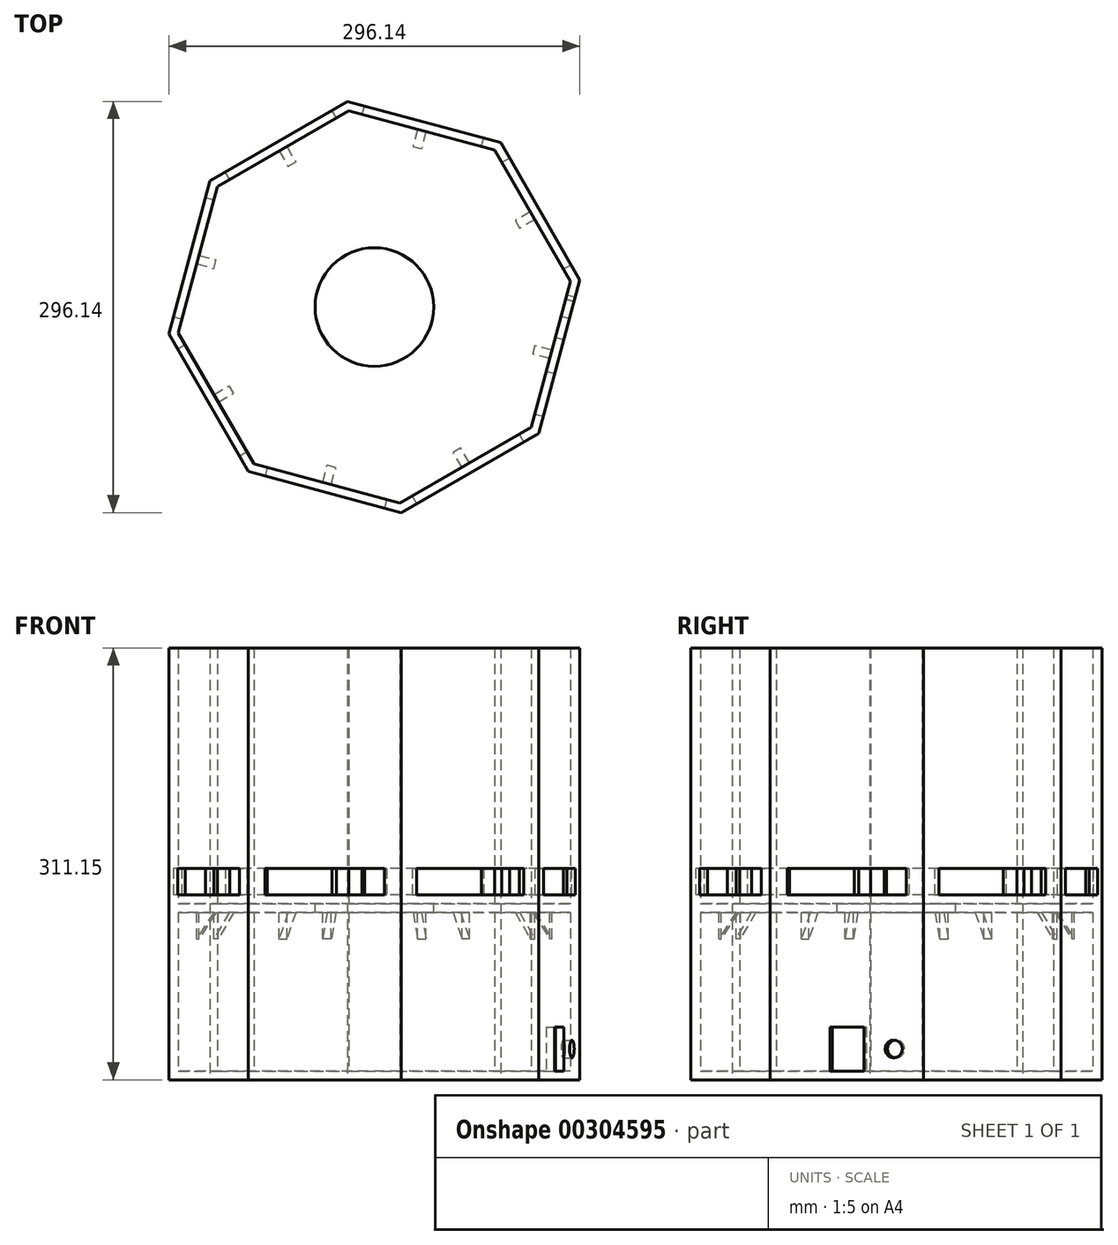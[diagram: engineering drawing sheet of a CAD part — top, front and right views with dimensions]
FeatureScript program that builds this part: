
annotation { "Feature Type Name" : "Feature", "Feature Type Description" : "" }
export const myFeature = defineFeature(function(context is Context, id is Id, definition is map)
    precondition{}
    {
        {
            var Q0;
            Q0=qCreatedBy(makeId("Top.planeOp"),FACE);
            var sketch = newSketch(context, id + "F0", { "sketchPlane" : qUnion([Q0])});
            skCircle(sketch, "E0.cCircle", {"center": v(0, 0) * mm, "radius": 137.97 * mm, "construction": true});
            skLineSegment(sketch, "E0.0", {"start": v(118.45, -90.95) * mm, "end": v(19.44, -148.07) * mm});
            skLineSegment(sketch, "E0.1", {"start": v(19.44, -148.07) * mm, "end": v(-90.95, -118.45) * mm});
            skLineSegment(sketch, "E0.2", {"start": v(-90.95, -118.45) * mm, "end": v(-148.07, -19.44) * mm});
            skLineSegment(sketch, "E0.3", {"start": v(-148.07, -19.44) * mm, "end": v(-118.45, 90.95) * mm});
            skLineSegment(sketch, "E0.4", {"start": v(-118.45, 90.95) * mm, "end": v(-19.44, 148.07) * mm});
            skLineSegment(sketch, "E0.5", {"start": v(-19.44, 148.07) * mm, "end": v(90.95, 118.45) * mm});
            skLineSegment(sketch, "E0.6", {"start": v(90.95, 118.45) * mm, "end": v(148.07, 19.44) * mm});
            skLineSegment(sketch, "E0.7", {"start": v(148.07, 19.44) * mm, "end": v(118.45, -90.95) * mm});
            skPoint(sketch, "E0.0.midPoint", {"position": v(68.94, -119.51) * mm});
            skCircle(sketch, "E1.cCircle", {"center": v(0, 0) * mm, "radius": 131.62 * mm, "construction": true});
            skLineSegment(sketch, "E1.0", {"start": v(113, -86.77) * mm, "end": v(18.55, -141.25) * mm});
            skLineSegment(sketch, "E1.1", {"start": v(18.55, -141.25) * mm, "end": v(-86.77, -113) * mm});
            skLineSegment(sketch, "E1.2", {"start": v(-86.77, -113) * mm, "end": v(-141.25, -18.55) * mm});
            skLineSegment(sketch, "E1.3", {"start": v(-141.25, -18.55) * mm, "end": v(-113, 86.77) * mm});
            skLineSegment(sketch, "E1.4", {"start": v(-113, 86.77) * mm, "end": v(-18.55, 141.25) * mm});
            skLineSegment(sketch, "E1.5", {"start": v(-18.55, 141.25) * mm, "end": v(86.77, 113) * mm});
            skLineSegment(sketch, "E1.6", {"start": v(86.77, 113) * mm, "end": v(141.25, 18.55) * mm});
            skLineSegment(sketch, "E1.7", {"start": v(141.25, 18.55) * mm, "end": v(113, -86.77) * mm});
            skPoint(sketch, "E1.0.midPoint", {"position": v(65.77, -114.01) * mm});
            skLineSegment(sketch, "E2", {"start": v(-19.44, 148.07) * mm, "end": v(0, 0) * mm});
            skSolve(sketch);
        }
        {
            var Q0;
            Q0=makeQuery(id+"F0.imprint","IMPRINT",FACE,{"disambiguationData":[TD([[makeQuery(id+"F0.imprint","IMPRINT",EDGE,{"derivedFrom":sQuery(id+"F0.wireOp",EDGE,"E1.0")}),-1.0]])]});
            cPlane(context, id + "F1", {"entities" : qUnion([Q0]), "cplaneType" : CPlaneType.OFFSET, "offset" : 120.65 * mm, "width" : 152.4 * mm, "height" : 152.4 * mm});
        }
        {
            var Q0;
            Q0=qCreatedBy(id+"F1.planeOp",FACE);
            var sketch = newSketch(context, id + "F2", { "sketchPlane" : qUnion([Q0])});
            skCircle(sketch, "E3.cCircle", {"center": v(0, 0) * mm, "radius": 137.97 * mm, "construction": true});
            skLineSegment(sketch, "E3.0", {"start": v(118.45, -90.95) * mm, "end": v(19.44, -148.07) * mm});
            skLineSegment(sketch, "E3.1", {"start": v(19.44, -148.07) * mm, "end": v(-90.95, -118.45) * mm});
            skLineSegment(sketch, "E3.2", {"start": v(-90.95, -118.45) * mm, "end": v(-148.07, -19.44) * mm});
            skLineSegment(sketch, "E3.3", {"start": v(-148.07, -19.44) * mm, "end": v(-118.45, 90.95) * mm});
            skLineSegment(sketch, "E3.4", {"start": v(-118.45, 90.95) * mm, "end": v(-19.44, 148.07) * mm});
            skLineSegment(sketch, "E3.5", {"start": v(-19.44, 148.07) * mm, "end": v(90.95, 118.45) * mm});
            skLineSegment(sketch, "E3.6", {"start": v(90.95, 118.45) * mm, "end": v(148.07, 19.44) * mm});
            skLineSegment(sketch, "E3.7", {"start": v(148.07, 19.44) * mm, "end": v(118.45, -90.95) * mm});
            skPoint(sketch, "E3.0.midPoint", {"position": v(68.94, -119.51) * mm});
            skCircle(sketch, "E4.cCircle", {"center": v(0, 0) * mm, "radius": 131.62 * mm, "construction": true});
            skLineSegment(sketch, "E4.0", {"start": v(113, -86.77) * mm, "end": v(18.55, -141.25) * mm});
            skLineSegment(sketch, "E4.1", {"start": v(18.55, -141.25) * mm, "end": v(-86.77, -113) * mm});
            skLineSegment(sketch, "E4.2", {"start": v(-86.77, -113) * mm, "end": v(-141.25, -18.55) * mm});
            skLineSegment(sketch, "E4.3", {"start": v(-141.25, -18.55) * mm, "end": v(-113, 86.77) * mm});
            skLineSegment(sketch, "E4.4", {"start": v(-113, 86.77) * mm, "end": v(-18.55, 141.25) * mm});
            skLineSegment(sketch, "E4.5", {"start": v(-18.55, 141.25) * mm, "end": v(86.77, 113) * mm});
            skLineSegment(sketch, "E4.6", {"start": v(86.77, 113) * mm, "end": v(141.25, 18.55) * mm});
            skLineSegment(sketch, "E4.7", {"start": v(141.25, 18.55) * mm, "end": v(113, -86.77) * mm});
            skPoint(sketch, "E4.0.midPoint", {"position": v(65.77, -114.01) * mm});
            skLineSegment(sketch, "E5", {"start": v(-19.44, 148.07) * mm, "end": v(0, 0) * mm});
            skSolve(sketch);
        }
        {
            var Q0;
            Q0=makeQuery(id+"F2.imprint","IMPRINT",FACE,{"disambiguationData":[TD([[makeQuery(id+"F2.imprint","IMPRINT",EDGE,{"derivedFrom":sQuery(id+"F2.wireOp",EDGE,"E4.0")}),-1.0]])]});
            extrude(context, id + "F3", {"entities" : qUnion([Q0]), "depth" : 6.35 * mm});
        }
        {
            var Q0;
            Q0=makeQuery(id+"F0.imprint","IMPRINT",FACE,{"disambiguationData":[TD([[makeQuery(id+"F0.imprint","IMPRINT",EDGE,{"derivedFrom":sQuery(id+"F0.wireOp",EDGE,"E1.0")}),-1.0]])]});
            extrude(context, id + "F4", {"entities" : qUnion([Q0]), "depth" : 6.35 * mm});
        }
        {
            var Q0;
            Q0=makeQuery(id+"F0.imprint","IMPRINT",FACE,{"disambiguationData":[TD([[makeQuery(id+"F0.imprint","IMPRINT",EDGE,{"derivedFrom":sQuery(id+"F0.wireOp",EDGE,"E0.0")}),-1.0]])]});
            extrude(context, id + "F5", {"entities" : qUnion([Q0]), "operationType" : NewBodyOperationType.ADD, "depth" : 311.15 * mm});
        }
        {
            var Q0;
            Q0=makeQuery(id+"F5.opExtrude","SWEPT_FACE",FACE,{"disambiguationData":[OSD([sQuery(id+"F0.wireOp",EDGE,"E0.1")])]});
            var sketch = newSketch(context, id + "F6", { "sketchPlane" : qUnion([Q0])});
            skLineSegment(sketch, "E6.bottom", {"start": v(-44.45, 152.4) * mm, "end": v(44.45, 152.4) * mm});
            skLineSegment(sketch, "E6.top", {"start": v(-44.45, 133.35) * mm, "end": v(44.45, 133.35) * mm});
            skLineSegment(sketch, "E6.left", {"start": v(-44.45, 152.4) * mm, "end": v(-44.45, 133.35) * mm});
            skLineSegment(sketch, "E6.right", {"start": v(44.45, 152.4) * mm, "end": v(44.45, 133.35) * mm});
            skSolve(sketch);
        }
        {
            var Q0;
            Q0=makeQuery(id+"F5.opExtrude","SWEPT_FACE",FACE,{"disambiguationData":[OSD([sQuery(id+"F0.wireOp",EDGE,"E0.2")])]});
            var sketch = newSketch(context, id + "F7", { "sketchPlane" : qUnion([Q0])});
            skLineSegment(sketch, "E7.bottom", {"start": v(-44.45, 152.4) * mm, "end": v(44.45, 152.4) * mm});
            skLineSegment(sketch, "E7.top", {"start": v(-44.45, 133.35) * mm, "end": v(44.45, 133.35) * mm});
            skLineSegment(sketch, "E7.left", {"start": v(-44.45, 152.4) * mm, "end": v(-44.45, 133.35) * mm});
            skLineSegment(sketch, "E7.right", {"start": v(44.45, 152.4) * mm, "end": v(44.45, 133.35) * mm});
            skSolve(sketch);
        }
        {
            var Q0;
            Q0=makeQuery(id+"F5.opExtrude","SWEPT_FACE",FACE,{"disambiguationData":[OSD([sQuery(id+"F0.wireOp",EDGE,"E0.3")])]});
            var sketch = newSketch(context, id + "F8", { "sketchPlane" : qUnion([Q0])});
            skLineSegment(sketch, "E8.bottom", {"start": v(-44.45, 152.4) * mm, "end": v(44.45, 152.4) * mm});
            skLineSegment(sketch, "E8.top", {"start": v(-44.45, 133.35) * mm, "end": v(44.45, 133.35) * mm});
            skLineSegment(sketch, "E8.left", {"start": v(-44.45, 152.4) * mm, "end": v(-44.45, 133.35) * mm});
            skLineSegment(sketch, "E8.right", {"start": v(44.45, 152.4) * mm, "end": v(44.45, 133.35) * mm});
            skSolve(sketch);
        }
        {
            var Q0;
            Q0=makeQuery(id+"F5.opExtrude","SWEPT_FACE",FACE,{"disambiguationData":[OSD([sQuery(id+"F0.wireOp",EDGE,"E0.4")])]});
            var sketch = newSketch(context, id + "F9", { "sketchPlane" : qUnion([Q0])});
            skLineSegment(sketch, "E9.bottom", {"start": v(-44.45, 152.4) * mm, "end": v(44.45, 152.4) * mm});
            skLineSegment(sketch, "E9.top", {"start": v(-44.45, 133.35) * mm, "end": v(44.45, 133.35) * mm});
            skLineSegment(sketch, "E9.left", {"start": v(-44.45, 152.4) * mm, "end": v(-44.45, 133.35) * mm});
            skLineSegment(sketch, "E9.right", {"start": v(44.45, 152.4) * mm, "end": v(44.45, 133.35) * mm});
            skSolve(sketch);
        }
        {
            var Q0;
            Q0=makeQuery(id+"F5.opExtrude","SWEPT_FACE",FACE,{"disambiguationData":[OSD([sQuery(id+"F0.wireOp",EDGE,"E0.5")])]});
            var sketch = newSketch(context, id + "F10", { "sketchPlane" : qUnion([Q0])});
            skLineSegment(sketch, "E10.bottom", {"start": v(-44.45, 152.4) * mm, "end": v(44.45, 152.4) * mm});
            skLineSegment(sketch, "E10.top", {"start": v(-44.45, 133.35) * mm, "end": v(44.45, 133.35) * mm});
            skLineSegment(sketch, "E10.left", {"start": v(-44.45, 152.4) * mm, "end": v(-44.45, 133.35) * mm});
            skLineSegment(sketch, "E10.right", {"start": v(44.45, 152.4) * mm, "end": v(44.45, 133.35) * mm});
            skSolve(sketch);
        }
        {
            var Q0;
            Q0=makeQuery(id+"F5.opExtrude","SWEPT_FACE",FACE,{"disambiguationData":[OSD([sQuery(id+"F0.wireOp",EDGE,"E0.6")])]});
            var sketch = newSketch(context, id + "F11", { "sketchPlane" : qUnion([Q0])});
            skLineSegment(sketch, "E11.bottom", {"start": v(-44.45, 152.4) * mm, "end": v(44.45, 152.4) * mm});
            skLineSegment(sketch, "E11.top", {"start": v(-44.45, 133.35) * mm, "end": v(44.45, 133.35) * mm});
            skLineSegment(sketch, "E11.left", {"start": v(-44.45, 152.4) * mm, "end": v(-44.45, 133.35) * mm});
            skLineSegment(sketch, "E11.right", {"start": v(44.45, 152.4) * mm, "end": v(44.45, 133.35) * mm});
            skSolve(sketch);
        }
        {
            var Q0;
            Q0=makeQuery(id+"F5.opExtrude","SWEPT_FACE",FACE,{"disambiguationData":[OSD([sQuery(id+"F0.wireOp",EDGE,"E0.7")])]});
            var sketch = newSketch(context, id + "F12", { "sketchPlane" : qUnion([Q0])});
            skLineSegment(sketch, "E12.bottom", {"start": v(-44.45, 152.4) * mm, "end": v(44.45, 152.4) * mm});
            skLineSegment(sketch, "E12.top", {"start": v(-44.45, 133.35) * mm, "end": v(44.45, 133.35) * mm});
            skLineSegment(sketch, "E12.left", {"start": v(-44.45, 152.4) * mm, "end": v(-44.45, 133.35) * mm});
            skLineSegment(sketch, "E12.right", {"start": v(44.45, 152.4) * mm, "end": v(44.45, 133.35) * mm});
            skSolve(sketch);
        }
        {
            var Q0;
            Q0=makeQuery(id+"F5.opExtrude","SWEPT_FACE",FACE,{"disambiguationData":[OSD([sQuery(id+"F0.wireOp",EDGE,"E0.0")])]});
            var sketch = newSketch(context, id + "F13", { "sketchPlane" : qUnion([Q0])});
            skLineSegment(sketch, "E13.bottom", {"start": v(-44.45, 152.4) * mm, "end": v(44.45, 152.4) * mm});
            skLineSegment(sketch, "E13.top", {"start": v(-44.45, 133.35) * mm, "end": v(44.45, 133.35) * mm});
            skLineSegment(sketch, "E13.left", {"start": v(-44.45, 152.4) * mm, "end": v(-44.45, 133.35) * mm});
            skLineSegment(sketch, "E13.right", {"start": v(44.45, 152.4) * mm, "end": v(44.45, 133.35) * mm});
            skSolve(sketch);
        }
        {
            var Q0;
            Q0=makeQuery(id+"F13.imprint","IMPRINT",FACE,{"disambiguationData":[TD([[makeQuery(id+"F13.imprint","IMPRINT",EDGE,{"derivedFrom":sQuery(id+"F13.wireOp",EDGE,"E13.bottom")}),-1.0]])]});
            extrude(context, id + "F14", {"entities" : qUnion([Q0]), "operationType" : NewBodyOperationType.REMOVE, "oppositeDirection" : true, "depth" : 25.4 * mm});
        }
        {
            var Q0;
            Q0=makeQuery(id+"F12.imprint","IMPRINT",FACE,{"disambiguationData":[TD([[makeQuery(id+"F12.imprint","IMPRINT",EDGE,{"derivedFrom":sQuery(id+"F12.wireOp",EDGE,"E12.bottom")}),-1.0]])]});
            extrude(context, id + "F15", {"entities" : qUnion([Q0]), "operationType" : NewBodyOperationType.REMOVE, "oppositeDirection" : true, "depth" : 25.4 * mm});
        }
        {
            var Q0;
            Q0=makeQuery(id+"F11.imprint","IMPRINT",FACE,{"disambiguationData":[TD([[makeQuery(id+"F11.imprint","IMPRINT",EDGE,{"derivedFrom":sQuery(id+"F11.wireOp",EDGE,"E11.bottom")}),-1.0]])]});
            extrude(context, id + "F16", {"entities" : qUnion([Q0]), "operationType" : NewBodyOperationType.REMOVE, "oppositeDirection" : true, "depth" : 25.4 * mm});
        }
        {
            var Q0;
            Q0=makeQuery(id+"F10.imprint","IMPRINT",FACE,{"disambiguationData":[TD([[makeQuery(id+"F10.imprint","IMPRINT",EDGE,{"derivedFrom":sQuery(id+"F10.wireOp",EDGE,"E10.bottom")}),-1.0]])]});
            extrude(context, id + "F17", {"entities" : qUnion([Q0]), "operationType" : NewBodyOperationType.REMOVE, "oppositeDirection" : true, "depth" : 25.4 * mm});
        }
        {
            var Q0;
            Q0=makeQuery(id+"F9.imprint","IMPRINT",FACE,{"disambiguationData":[TD([[makeQuery(id+"F9.imprint","IMPRINT",EDGE,{"derivedFrom":sQuery(id+"F9.wireOp",EDGE,"E9.bottom")}),-1.0]])]});
            extrude(context, id + "F18", {"entities" : qUnion([Q0]), "operationType" : NewBodyOperationType.REMOVE, "oppositeDirection" : true, "depth" : 25.4 * mm});
        }
        {
            var Q0;
            Q0=makeQuery(id+"F8.imprint","IMPRINT",FACE,{"disambiguationData":[TD([[makeQuery(id+"F8.imprint","IMPRINT",EDGE,{"derivedFrom":sQuery(id+"F8.wireOp",EDGE,"E8.bottom")}),-1.0]])]});
            extrude(context, id + "F19", {"entities" : qUnion([Q0]), "operationType" : NewBodyOperationType.REMOVE, "oppositeDirection" : true, "depth" : 25.4 * mm});
        }
        {
            var Q0;
            Q0=makeQuery(id+"F7.imprint","IMPRINT",FACE,{"disambiguationData":[TD([[makeQuery(id+"F7.imprint","IMPRINT",EDGE,{"derivedFrom":sQuery(id+"F7.wireOp",EDGE,"E7.bottom")}),-1.0]])]});
            extrude(context, id + "F20", {"entities" : qUnion([Q0]), "operationType" : NewBodyOperationType.REMOVE, "oppositeDirection" : true, "depth" : 25.4 * mm});
        }
        {
            var Q0;
            Q0=makeQuery(id+"F6.imprint","IMPRINT",FACE,{"disambiguationData":[TD([[makeQuery(id+"F6.imprint","IMPRINT",EDGE,{"derivedFrom":sQuery(id+"F6.wireOp",EDGE,"E6.bottom")}),-1.0]])]});
            extrude(context, id + "F21", {"entities" : qUnion([Q0]), "operationType" : NewBodyOperationType.REMOVE, "oppositeDirection" : true, "depth" : 25.4 * mm});
        }
        {
            var Q0;
            Q0=makeQuery(id+"F3.opExtrude","CAP_FACE",FACE,{"disambiguationData":[OSD([sQuery(id+"F2.wireOp",EDGE,"E4.0"),sQuery(id+"F2.wireOp",EDGE,"E4.1"),sQuery(id+"F2.wireOp",EDGE,"E4.2"),sQuery(id+"F2.wireOp",EDGE,"E4.3"),sQuery(id+"F2.wireOp",EDGE,"E4.4"),sQuery(id+"F2.wireOp",EDGE,"E4.5"),sQuery(id+"F2.wireOp",EDGE,"E4.6"),sQuery(id+"F2.wireOp",EDGE,"E4.7")])],"isStart":false});
            var sketch = newSketch(context, id + "F22", { "sketchPlane" : qUnion([Q0])});
            skCircle(sketch, "E14", {"center": v(0, 0) * mm, "radius": 42.72 * mm});
            skSolve(sketch);
        }
        {
            var Q0;
            Q0=makeQuery(id+"F22.imprint","IMPRINT",FACE,{"disambiguationData":[TD([[makeQuery(id+"F22.imprint","IMPRINT",EDGE,{"derivedFrom":sQuery(id+"F22.wireOp",EDGE,"E14")}),1.0]])]});
            extrude(context, id + "F23", {"entities" : qUnion([Q0]), "operationType" : NewBodyOperationType.REMOVE, "oppositeDirection" : true, "depth" : 25.4 * mm});
        }
        {
            var Q0;
            Q0=makeQuery(id+"F5.opExtrude","SWEPT_FACE",FACE,{"disambiguationData":[OSD([sQuery(id+"F0.wireOp",EDGE,"E0.7")])]});
            var sketch = newSketch(context, id + "F24", { "sketchPlane" : qUnion([Q0])});
            skLineSegment(sketch, "E15.bottom", {"start": v(-12.7, 38.1) * mm, "end": v(12.7, 38.1) * mm});
            skLineSegment(sketch, "E15.top", {"start": v(-12.7, 6.35) * mm, "end": v(12.7, 6.35) * mm});
            skLineSegment(sketch, "E15.left", {"start": v(-12.7, 38.1) * mm, "end": v(-12.7, 6.35) * mm});
            skLineSegment(sketch, "E15.right", {"start": v(12.7, 38.1) * mm, "end": v(12.7, 6.35) * mm});
            skLineSegment(sketch, "E16", {"start": v(-12.7, 38.1) * mm, "end": v(-57.15, 38.1) * mm});
            skLineSegment(sketch, "E17", {"start": v(12.7, 38.1) * mm, "end": v(57.15, 38.1) * mm});
            skCircle(sketch, "E18", {"center": v(34.93, 22.23) * mm, "radius": 6.35 * mm});
            skPoint(sketch, "E18.centerSnap0", {"position": v(12.7, 22.23) * mm});
            skLineSegment(sketch, "E19", {"start": v(34.93, 22.23) * mm, "end": v(12.7, 22.23) * mm});
            skLineSegment(sketch, "E20", {"start": v(34.93, 22.23) * mm, "end": v(57.15, 22.23) * mm});
            skLineSegment(sketch, "E21", {"start": v(34.93, 22.23) * mm, "end": v(34.93, 38.1) * mm});
            skLineSegment(sketch, "E22", {"start": v(34.93, 22.23) * mm, "end": v(34.93, 6.35) * mm});
            skSolve(sketch);
        }
        {
            var Q0;
            Q0=makeQuery(id+"F24.imprint","IMPRINT",FACE,{"disambiguationData":[TD([[makeQuery(id+"F24.imprint","IMPRINT",EDGE,{"derivedFrom":sQuery(id+"F24.wireOp",EDGE,"E15.bottom")}),-1.0]])]});
            extrude(context, id + "F25", {"entities" : qUnion([Q0]), "operationType" : NewBodyOperationType.REMOVE, "oppositeDirection" : true, "depth" : 25.4 * mm});
        }
        {
            var Q0;
            {var subQ0=sQuery(id+"F24.wireOp",EDGE,"E21");var subQ1=sQuery(id+"F24.wireOp",EDGE,"E18");var subQ2=makeQuery(id+"F24.imprint","INTERSECT",VERTEX,{"derivedFrom":[subQ1,subQ0]});Q0=makeQuery(id+"F24.imprint","IMPRINT",FACE,{"disambiguationData":[TD([[makeQuery(id+"F24.imprint","IMPRINT",EDGE,{"disambiguationData":[TD([[subQ2,1.0]])],"derivedFrom":subQ1}),1.0]])]});}
            var Q1;
            {var subQ0=sQuery(id+"F24.wireOp",EDGE,"E21");var subQ1=sQuery(id+"F24.wireOp",EDGE,"E18");var subQ2=makeQuery(id+"F24.imprint","INTERSECT",VERTEX,{"derivedFrom":[subQ1,subQ0]});Q1=makeQuery(id+"F24.imprint","IMPRINT",FACE,{"disambiguationData":[TD([[makeQuery(id+"F24.imprint","IMPRINT",EDGE,{"disambiguationData":[TD([[subQ2,-1.0]])],"derivedFrom":subQ1}),1.0]])]});}
            var Q2;
            {var subQ0=sQuery(id+"F24.wireOp",EDGE,"E22");var subQ1=sQuery(id+"F24.wireOp",EDGE,"E18");var subQ2=makeQuery(id+"F24.imprint","INTERSECT",VERTEX,{"derivedFrom":[subQ1,subQ0]});Q2=makeQuery(id+"F24.imprint","IMPRINT",FACE,{"disambiguationData":[TD([[makeQuery(id+"F24.imprint","IMPRINT",EDGE,{"disambiguationData":[TD([[subQ2,1.0]])],"derivedFrom":subQ1}),1.0]])]});}
            var Q3;
            {var subQ0=sQuery(id+"F24.wireOp",EDGE,"E22");var subQ1=sQuery(id+"F24.wireOp",EDGE,"E18");var subQ2=makeQuery(id+"F24.imprint","INTERSECT",VERTEX,{"derivedFrom":[subQ1,subQ0]});Q3=makeQuery(id+"F24.imprint","IMPRINT",FACE,{"disambiguationData":[TD([[makeQuery(id+"F24.imprint","IMPRINT",EDGE,{"disambiguationData":[TD([[subQ2,-1.0]])],"derivedFrom":subQ1}),1.0]])]});}
            extrude(context, id + "F26", {"entities" : qUnion([Q0, Q1, Q2, Q3]), "operationType" : NewBodyOperationType.REMOVE, "oppositeDirection" : true, "depth" : 25.4 * mm});
        }
        {
            var Q0;
            Q0=makeQuery(id+"F5.opExtrude","SWEPT_FACE",FACE,{"disambiguationData":[OSD([sQuery(id+"F0.wireOp",EDGE,"E1.6")])]});
            var sketch = newSketch(context, id + "F27", { "sketchPlane" : qUnion([Q0])});
            skLineSegment(sketch, "E23.bottom", {"start": v(-3.17, 120.65) * mm, "end": v(3.18, 120.65) * mm});
            skLineSegment(sketch, "E23.top", {"start": v(-3.17, 101.6) * mm, "end": v(3.18, 101.6) * mm});
            skLineSegment(sketch, "E23.left", {"start": v(-3.17, 120.65) * mm, "end": v(-3.17, 101.6) * mm});
            skLineSegment(sketch, "E23.right", {"start": v(3.18, 120.65) * mm, "end": v(3.18, 101.6) * mm});
            skLineSegment(sketch, "E24", {"start": v(3.18, 111.12) * mm, "end": v(54.52, 111.12) * mm});
            skLineSegment(sketch, "E25", {"start": v(-3.17, 111.12) * mm, "end": v(-54.52, 111.12) * mm});
            skSolve(sketch);
        }
        {
            var Q0;
            Q0=makeQuery(id+"F5.opExtrude","SWEPT_FACE",FACE,{"disambiguationData":[OSD([sQuery(id+"F0.wireOp",EDGE,"E1.7")])]});
            var sketch = newSketch(context, id + "F28", { "sketchPlane" : qUnion([Q0])});
            skLineSegment(sketch, "E26.bottom", {"start": v(-3.17, 120.65) * mm, "end": v(3.18, 120.65) * mm});
            skLineSegment(sketch, "E26.top", {"start": v(-3.17, 101.6) * mm, "end": v(3.18, 101.6) * mm});
            skLineSegment(sketch, "E26.left", {"start": v(-3.18, 120.65) * mm, "end": v(-3.18, 101.6) * mm});
            skLineSegment(sketch, "E26.right", {"start": v(3.18, 120.65) * mm, "end": v(3.18, 101.6) * mm});
            skLineSegment(sketch, "E27", {"start": v(3.18, 111.12) * mm, "end": v(54.52, 111.12) * mm});
            skLineSegment(sketch, "E28", {"start": v(-3.17, 111.12) * mm, "end": v(-54.52, 111.12) * mm});
            skSolve(sketch);
        }
        {
            var Q0;
            Q0=makeQuery(id+"F5.opExtrude","SWEPT_FACE",FACE,{"disambiguationData":[OSD([sQuery(id+"F0.wireOp",EDGE,"E1.0")])]});
            var sketch = newSketch(context, id + "F29", { "sketchPlane" : qUnion([Q0])});
            skLineSegment(sketch, "E29.bottom", {"start": v(-3.17, 120.65) * mm, "end": v(3.18, 120.65) * mm});
            skLineSegment(sketch, "E29.top", {"start": v(-3.17, 101.6) * mm, "end": v(3.18, 101.6) * mm});
            skLineSegment(sketch, "E29.left", {"start": v(-3.17, 120.65) * mm, "end": v(-3.17, 101.6) * mm});
            skLineSegment(sketch, "E29.right", {"start": v(3.18, 120.65) * mm, "end": v(3.18, 101.6) * mm});
            skLineSegment(sketch, "E30", {"start": v(3.18, 111.12) * mm, "end": v(54.52, 111.12) * mm});
            skLineSegment(sketch, "E31", {"start": v(-3.17, 111.12) * mm, "end": v(-54.52, 111.12) * mm});
            skSolve(sketch);
        }
        {
            var Q0;
            Q0=makeQuery(id+"F5.opExtrude","SWEPT_FACE",FACE,{"disambiguationData":[OSD([sQuery(id+"F0.wireOp",EDGE,"E1.1")])]});
            var sketch = newSketch(context, id + "F30", { "sketchPlane" : qUnion([Q0])});
            skLineSegment(sketch, "E32.bottom", {"start": v(-3.17, 120.65) * mm, "end": v(3.18, 120.65) * mm});
            skLineSegment(sketch, "E32.top", {"start": v(-3.17, 101.6) * mm, "end": v(3.18, 101.6) * mm});
            skLineSegment(sketch, "E32.left", {"start": v(-3.17, 120.65) * mm, "end": v(-3.17, 101.6) * mm});
            skLineSegment(sketch, "E32.right", {"start": v(3.18, 120.65) * mm, "end": v(3.18, 101.6) * mm});
            skLineSegment(sketch, "E33", {"start": v(3.18, 111.12) * mm, "end": v(54.52, 111.12) * mm});
            skLineSegment(sketch, "E34", {"start": v(-3.17, 111.12) * mm, "end": v(-54.52, 111.12) * mm});
            skSolve(sketch);
        }
        {
            var Q0;
            Q0=makeQuery(id+"F5.opExtrude","SWEPT_FACE",FACE,{"disambiguationData":[OSD([sQuery(id+"F0.wireOp",EDGE,"E1.2")])]});
            var sketch = newSketch(context, id + "F31", { "sketchPlane" : qUnion([Q0])});
            skLineSegment(sketch, "E35.bottom", {"start": v(-3.17, 120.65) * mm, "end": v(3.18, 120.65) * mm});
            skLineSegment(sketch, "E35.top", {"start": v(-3.17, 101.6) * mm, "end": v(3.18, 101.6) * mm});
            skLineSegment(sketch, "E35.left", {"start": v(-3.17, 120.65) * mm, "end": v(-3.17, 101.6) * mm});
            skLineSegment(sketch, "E35.right", {"start": v(3.18, 120.65) * mm, "end": v(3.18, 101.6) * mm});
            skLineSegment(sketch, "E36", {"start": v(3.18, 111.12) * mm, "end": v(54.52, 111.13) * mm});
            skLineSegment(sketch, "E37", {"start": v(-3.17, 111.12) * mm, "end": v(-54.52, 111.12) * mm});
            skSolve(sketch);
        }
        {
            var Q0;
            Q0=makeQuery(id+"F5.opExtrude","SWEPT_FACE",FACE,{"disambiguationData":[OSD([sQuery(id+"F0.wireOp",EDGE,"E1.3")])]});
            var sketch = newSketch(context, id + "F32", { "sketchPlane" : qUnion([Q0])});
            skLineSegment(sketch, "E38.bottom", {"start": v(-3.17, 120.65) * mm, "end": v(3.18, 120.65) * mm});
            skLineSegment(sketch, "E38.top", {"start": v(-3.17, 101.6) * mm, "end": v(3.18, 101.6) * mm});
            skLineSegment(sketch, "E38.left", {"start": v(-3.17, 120.65) * mm, "end": v(-3.17, 101.6) * mm});
            skLineSegment(sketch, "E38.right", {"start": v(3.18, 120.65) * mm, "end": v(3.18, 101.6) * mm});
            skLineSegment(sketch, "E39", {"start": v(3.18, 111.12) * mm, "end": v(54.52, 111.13) * mm});
            skLineSegment(sketch, "E40", {"start": v(-3.17, 111.12) * mm, "end": v(-54.52, 111.12) * mm});
            skSolve(sketch);
        }
        {
            var Q0;
            Q0=makeQuery(id+"F5.opExtrude","SWEPT_FACE",FACE,{"disambiguationData":[OSD([sQuery(id+"F0.wireOp",EDGE,"E1.4")])]});
            var sketch = newSketch(context, id + "F33", { "sketchPlane" : qUnion([Q0])});
            skLineSegment(sketch, "E41.bottom", {"start": v(-3.17, 120.65) * mm, "end": v(3.18, 120.65) * mm});
            skLineSegment(sketch, "E41.top", {"start": v(-3.17, 101.6) * mm, "end": v(3.18, 101.6) * mm});
            skLineSegment(sketch, "E41.left", {"start": v(-3.17, 120.65) * mm, "end": v(-3.17, 101.6) * mm});
            skLineSegment(sketch, "E41.right", {"start": v(3.18, 120.65) * mm, "end": v(3.18, 101.6) * mm});
            skLineSegment(sketch, "E42", {"start": v(3.18, 111.12) * mm, "end": v(54.52, 111.12) * mm});
            skLineSegment(sketch, "E43", {"start": v(-3.17, 111.12) * mm, "end": v(-54.52, 111.12) * mm});
            skSolve(sketch);
        }
        {
            var Q0;
            Q0=makeQuery(id+"F5.opExtrude","SWEPT_FACE",FACE,{"disambiguationData":[OSD([sQuery(id+"F0.wireOp",EDGE,"E1.5")])]});
            var sketch = newSketch(context, id + "F34", { "sketchPlane" : qUnion([Q0])});
            skLineSegment(sketch, "E44.bottom", {"start": v(-3.17, 120.65) * mm, "end": v(3.18, 120.65) * mm});
            skLineSegment(sketch, "E44.top", {"start": v(-3.17, 101.6) * mm, "end": v(3.18, 101.6) * mm});
            skLineSegment(sketch, "E44.left", {"start": v(-3.17, 120.65) * mm, "end": v(-3.17, 101.6) * mm});
            skLineSegment(sketch, "E44.right", {"start": v(3.18, 120.65) * mm, "end": v(3.18, 101.6) * mm});
            skLineSegment(sketch, "E45", {"start": v(3.18, 111.12) * mm, "end": v(54.52, 111.12) * mm});
            skLineSegment(sketch, "E46", {"start": v(-3.17, 111.12) * mm, "end": v(-54.52, 111.12) * mm});
            skSolve(sketch);
        }
        {
            var Q0;
            Q0=qCreatedBy(id+"F1.planeOp",FACE);
            var sketch = newSketch(context, id + "F35", { "sketchPlane" : qUnion([Q0])});
            skLineSegment(sketch, "E47", {"start": v(-62.17, 101.42) * mm, "end": v(-56.67, 104.6) * mm});
            skLineSegment(sketch, "E48", {"start": v(27.75, 115.68) * mm, "end": v(33.89, 114.04) * mm});
            skLineSegment(sketch, "E49", {"start": v(101.42, 62.17) * mm, "end": v(104.6, 56.67) * mm});
            skLineSegment(sketch, "E50", {"start": v(62.17, -101.42) * mm, "end": v(56.67, -104.6) * mm});
            skLineSegment(sketch, "E51", {"start": v(-101.42, -62.17) * mm, "end": v(-104.6, -56.67) * mm});
            skLineSegment(sketch, "E52", {"start": v(-115.68, 27.75) * mm, "end": v(-114.04, 33.89) * mm});
            skLineSegment(sketch, "E53", {"start": v(115.68, -27.75) * mm, "end": v(114.04, -33.89) * mm});
            skLineSegment(sketch, "E54", {"start": v(-33.89, -114.04) * mm, "end": v(-27.75, -115.68) * mm});
            skPoint(sketch, "E55", {"position": v(-126.3, 37.18) * mm});
            skPoint(sketch, "E56", {"position": v(-115.6, -63.02) * mm});
            skPoint(sketch, "E57", {"position": v(-37.18, -126.3) * mm});
            skPoint(sketch, "E58", {"position": v(126.3, -37.18) * mm});
            skPoint(sketch, "E59", {"position": v(115.6, 63.02) * mm});
            skPoint(sketch, "E60", {"position": v(37.18, 126.3) * mm});
            skPoint(sketch, "E61", {"position": v(-63.02, 115.6) * mm});
            skLineSegment(sketch, "E62", {"start": v(-126.3, 37.18) * mm, "end": v(-114.04, 33.89) * mm});
            skLineSegment(sketch, "E63", {"start": v(-115.6, -63.02) * mm, "end": v(-104.6, -56.67) * mm});
            skLineSegment(sketch, "E64", {"start": v(-33.89, -114.04) * mm, "end": v(-37.18, -126.3) * mm});
            skLineSegment(sketch, "E65", {"start": v(114.04, -33.89) * mm, "end": v(126.3, -37.18) * mm});
            skLineSegment(sketch, "E66", {"start": v(104.6, 56.67) * mm, "end": v(115.6, 63.02) * mm});
            skLineSegment(sketch, "E67", {"start": v(33.89, 114.04) * mm, "end": v(37.18, 126.3) * mm});
            skLineSegment(sketch, "E68", {"start": v(-56.67, 104.6) * mm, "end": v(-63.02, 115.6) * mm});
            skPoint(sketch, "E69", {"position": v(63.02, -115.6) * mm});
            skLineSegment(sketch, "E70", {"start": v(56.67, -104.6) * mm, "end": v(63.02, -115.6) * mm});
            skSolve(sketch);
        }
        {
            var Q0;
            Q0=sQuery(id+"F34.wireOp",VERTEX,"E44.top.end");
            var Q1;
            Q1=sQuery(id+"F35.wireOp",VERTEX,"E60");
            var Q2;
            Q2=sQuery(id+"F35.wireOp",VERTEX,"E48.end");
            cPlane(context, id + "F36", {"entities" : qUnion([Q0, Q1, Q2]), "cplaneType" : CPlaneType.THREE_POINT, "offset" : 25.4 * mm, "width" : 152.4 * mm, "height" : 152.4 * mm});
        }
        {
            var Q0;
            Q0=sQuery(id+"F33.wireOp",VERTEX,"E41.right.end");
            var Q1;
            Q1=sQuery(id+"F35.wireOp",VERTEX,"E61");
            var Q2;
            Q2=sQuery(id+"F35.wireOp",VERTEX,"E47.end");
            cPlane(context, id + "F37", {"entities" : qUnion([Q0, Q1, Q2]), "cplaneType" : CPlaneType.THREE_POINT, "offset" : 25.4 * mm, "width" : 152.4 * mm, "height" : 152.4 * mm});
        }
        {
            var Q0;
            Q0=sQuery(id+"F32.wireOp",VERTEX,"E38.top.end");
            var Q1;
            Q1=sQuery(id+"F35.wireOp",VERTEX,"E55");
            var Q2;
            Q2=sQuery(id+"F35.wireOp",VERTEX,"E62.end");
            cPlane(context, id + "F38", {"entities" : qUnion([Q0, Q1, Q2]), "cplaneType" : CPlaneType.THREE_POINT, "offset" : 25.4 * mm, "width" : 152.4 * mm, "height" : 152.4 * mm});
        }
        {
            var Q0;
            Q0=sQuery(id+"F31.wireOp",VERTEX,"E35.right.end");
            var Q1;
            Q1=sQuery(id+"F35.wireOp",VERTEX,"E56");
            var Q2;
            Q2=sQuery(id+"F35.wireOp",VERTEX,"E63.end");
            cPlane(context, id + "F39", {"entities" : qUnion([Q0, Q1, Q2]), "cplaneType" : CPlaneType.THREE_POINT, "offset" : 25.4 * mm, "width" : 152.4 * mm, "height" : 152.4 * mm});
        }
        {
            var Q0;
            Q0=sQuery(id+"F35.wireOp",VERTEX,"E57");
            var Q1;
            Q1=sQuery(id+"F35.wireOp",VERTEX,"E54.start");
            var Q2;
            Q2=sQuery(id+"F30.wireOp",VERTEX,"E32.right.end");
            cPlane(context, id + "F40", {"entities" : qUnion([Q0, Q1, Q2]), "cplaneType" : CPlaneType.THREE_POINT, "offset" : 25.4 * mm, "width" : 152.4 * mm, "height" : 152.4 * mm});
        }
        {
            var Q0;
            Q0=sQuery(id+"F35.wireOp",VERTEX,"E69");
            var Q1;
            Q1=sQuery(id+"F35.wireOp",VERTEX,"E70.start");
            var Q2;
            Q2=sQuery(id+"F29.wireOp",VERTEX,"E29.right.end");
            cPlane(context, id + "F41", {"entities" : qUnion([Q0, Q1, Q2]), "cplaneType" : CPlaneType.THREE_POINT, "offset" : 25.4 * mm, "width" : 152.4 * mm, "height" : 152.4 * mm});
        }
        {
            var Q0;
            Q0=sQuery(id+"F35.wireOp",VERTEX,"E65.start");
            var Q1;
            Q1=sQuery(id+"F35.wireOp",VERTEX,"E58");
            var Q2;
            Q2=sQuery(id+"F28.wireOp",VERTEX,"E26.right.end");
            cPlane(context, id + "F42", {"entities" : qUnion([Q0, Q1, Q2]), "cplaneType" : CPlaneType.THREE_POINT, "offset" : 25.4 * mm, "width" : 152.4 * mm, "height" : 152.4 * mm});
        }
        {
            var Q0;
            Q0=sQuery(id+"F27.wireOp",VERTEX,"E23.right.end");
            var Q1;
            Q1=sQuery(id+"F35.wireOp",VERTEX,"E59");
            var Q2;
            Q2=sQuery(id+"F35.wireOp",VERTEX,"E66.start");
            cPlane(context, id + "F43", {"entities" : qUnion([Q0, Q1, Q2]), "cplaneType" : CPlaneType.THREE_POINT, "offset" : 25.4 * mm, "width" : 152.4 * mm, "height" : 152.4 * mm});
        }
        {
            var Q0;
            Q0=qCreatedBy(id+"F36.planeOp",FACE);
            var sketch = newSketch(context, id + "F44", { "sketchPlane" : qUnion([Q0])});
            skPoint(sketch, "E71", {"position": v(-118.92, 120.65) * mm});
            skPoint(sketch, "E72", {"position": v(-131.62, 120.65) * mm});
            skPoint(sketch, "E73", {"position": v(-131.62, 101.6) * mm});
            skLineSegment(sketch, "E74", {"start": v(-118.92, 120.65) * mm, "end": v(-131.62, 101.6) * mm});
            skLineSegment(sketch, "E75", {"start": v(-131.62, 101.6) * mm, "end": v(-131.62, 120.65) * mm});
            skLineSegment(sketch, "E76", {"start": v(-131.62, 120.65) * mm, "end": v(-118.92, 120.65) * mm});
            skSolve(sketch);
        }
        {
            var Q0;
            Q0=qCreatedBy(id+"F37.planeOp",FACE);
            var sketch = newSketch(context, id + "F45", { "sketchPlane" : qUnion([Q0])});
            skPoint(sketch, "E77", {"position": v(-118.92, 120.65) * mm});
            skPoint(sketch, "E78", {"position": v(-131.62, 120.65) * mm});
            skPoint(sketch, "E79", {"position": v(-131.62, 101.6) * mm});
            skLineSegment(sketch, "E80", {"start": v(-118.92, 120.65) * mm, "end": v(-131.62, 101.6) * mm});
            skLineSegment(sketch, "E81", {"start": v(-131.62, 101.6) * mm, "end": v(-131.62, 120.65) * mm});
            skLineSegment(sketch, "E82", {"start": v(-131.62, 120.65) * mm, "end": v(-118.92, 120.65) * mm});
            skSolve(sketch);
        }
        {
            var Q0;
            Q0=qCreatedBy(id+"F38.planeOp",FACE);
            var sketch = newSketch(context, id + "F46", { "sketchPlane" : qUnion([Q0])});
            skPoint(sketch, "E83", {"position": v(-118.92, 120.65) * mm});
            skPoint(sketch, "E84", {"position": v(-131.62, 120.65) * mm});
            skPoint(sketch, "E85", {"position": v(-131.62, 101.6) * mm});
            skLineSegment(sketch, "E86", {"start": v(-118.92, 120.65) * mm, "end": v(-131.62, 101.6) * mm});
            skLineSegment(sketch, "E87", {"start": v(-131.62, 101.6) * mm, "end": v(-131.62, 120.65) * mm});
            skLineSegment(sketch, "E88", {"start": v(-131.62, 120.65) * mm, "end": v(-118.92, 120.65) * mm});
            skSolve(sketch);
        }
        {
            var Q0;
            Q0=qCreatedBy(id+"F39.planeOp",FACE);
            var sketch = newSketch(context, id + "F47", { "sketchPlane" : qUnion([Q0])});
            skPoint(sketch, "E89", {"position": v(-118.92, 120.65) * mm});
            skPoint(sketch, "E90", {"position": v(-131.62, 120.65) * mm});
            skPoint(sketch, "E91", {"position": v(-131.62, 101.6) * mm});
            skLineSegment(sketch, "E92", {"start": v(-118.92, 120.65) * mm, "end": v(-131.62, 101.6) * mm});
            skLineSegment(sketch, "E93", {"start": v(-131.62, 101.6) * mm, "end": v(-131.62, 120.65) * mm});
            skLineSegment(sketch, "E94", {"start": v(-131.62, 120.65) * mm, "end": v(-118.92, 120.65) * mm});
            skSolve(sketch);
        }
        {
            var Q0;
            Q0=qCreatedBy(id+"F40.planeOp",FACE);
            var sketch = newSketch(context, id + "F48", { "sketchPlane" : qUnion([Q0])});
            skPoint(sketch, "E95", {"position": v(-118.92, 120.65) * mm});
            skPoint(sketch, "E96", {"position": v(-131.62, 120.65) * mm});
            skPoint(sketch, "E97", {"position": v(-131.62, 101.6) * mm});
            skLineSegment(sketch, "E98", {"start": v(-118.92, 120.65) * mm, "end": v(-131.62, 101.6) * mm});
            skLineSegment(sketch, "E99", {"start": v(-131.62, 101.6) * mm, "end": v(-131.62, 120.65) * mm});
            skLineSegment(sketch, "E100", {"start": v(-131.62, 120.65) * mm, "end": v(-118.92, 120.65) * mm});
            skSolve(sketch);
        }
        {
            var Q0;
            Q0=qCreatedBy(id+"F41.planeOp",FACE);
            var sketch = newSketch(context, id + "F49", { "sketchPlane" : qUnion([Q0])});
            skPoint(sketch, "E101", {"position": v(-118.92, 120.65) * mm});
            skPoint(sketch, "E102", {"position": v(-131.62, 120.65) * mm});
            skPoint(sketch, "E103", {"position": v(-131.62, 101.6) * mm});
            skLineSegment(sketch, "E104", {"start": v(-118.92, 120.65) * mm, "end": v(-131.62, 101.6) * mm});
            skLineSegment(sketch, "E105", {"start": v(-131.62, 101.6) * mm, "end": v(-131.62, 120.65) * mm});
            skLineSegment(sketch, "E106", {"start": v(-131.62, 120.65) * mm, "end": v(-118.92, 120.65) * mm});
            skSolve(sketch);
        }
        {
            var Q0;
            Q0=qCreatedBy(id+"F42.planeOp",FACE);
            var sketch = newSketch(context, id + "F50", { "sketchPlane" : qUnion([Q0])});
            skPoint(sketch, "E107", {"position": v(144.32, 120.65) * mm});
            skPoint(sketch, "E108", {"position": v(131.62, 120.65) * mm});
            skPoint(sketch, "E109", {"position": v(131.62, 101.6) * mm});
            skLineSegment(sketch, "E110", {"start": v(144.32, 120.65) * mm, "end": v(131.62, 101.6) * mm});
            skLineSegment(sketch, "E111", {"start": v(131.62, 101.6) * mm, "end": v(131.62, 120.65) * mm});
            skLineSegment(sketch, "E112", {"start": v(131.62, 120.65) * mm, "end": v(144.32, 120.65) * mm});
            skLineSegment(sketch, "E113.MirrorCS", {"start": v(131.62, 120.65) * mm, "end": v(118.92, 120.65) * mm});
            skLineSegment(sketch, "E114.MirrorCS", {"start": v(118.92, 120.65) * mm, "end": v(131.62, 101.6) * mm});
            skPoint(sketch, "E115.MirrorP", {"position": v(118.92, 120.65) * mm});
            skSolve(sketch);
        }
        {
            var Q0;
            Q0=qCreatedBy(id+"F43.planeOp",FACE);
            var sketch = newSketch(context, id + "F51", { "sketchPlane" : qUnion([Q0])});
            skPoint(sketch, "E116", {"position": v(-118.92, 120.65) * mm});
            skPoint(sketch, "E117", {"position": v(-131.62, 120.65) * mm});
            skPoint(sketch, "E118", {"position": v(-131.62, 101.6) * mm});
            skLineSegment(sketch, "E119", {"start": v(-118.92, 120.65) * mm, "end": v(-131.62, 101.6) * mm});
            skLineSegment(sketch, "E120", {"start": v(-131.62, 101.6) * mm, "end": v(-131.62, 120.65) * mm});
            skLineSegment(sketch, "E121", {"start": v(-131.62, 120.65) * mm, "end": v(-118.92, 120.65) * mm});
            skSolve(sketch);
        }
        {
            var Q0;
            Q0=makeQuery(id+"F51.imprint","IMPRINT",FACE,{"disambiguationData":[TD([[makeQuery(id+"F51.imprint","IMPRINT",EDGE,{"derivedFrom":sQuery(id+"F51.wireOp",EDGE,"E119")}),-1.0]])]});
            extrude(context, id + "F52", {"entities" : qUnion([Q0]), "operationType" : NewBodyOperationType.ADD, "depth" : 6.35 * mm});
        }
        {
            var Q0;
            Q0=makeQuery(id+"F44.imprint","IMPRINT",FACE,{"disambiguationData":[TD([[makeQuery(id+"F44.imprint","IMPRINT",EDGE,{"derivedFrom":sQuery(id+"F44.wireOp",EDGE,"E74")}),-1.0]])]});
            extrude(context, id + "F53", {"entities" : qUnion([Q0]), "operationType" : NewBodyOperationType.ADD, "depth" : 6.35 * mm});
        }
        {
            var Q0;
            Q0=makeQuery(id+"F45.imprint","IMPRINT",FACE,{"disambiguationData":[TD([[makeQuery(id+"F45.imprint","IMPRINT",EDGE,{"derivedFrom":sQuery(id+"F45.wireOp",EDGE,"E80")}),-1.0]])]});
            extrude(context, id + "F54", {"entities" : qUnion([Q0]), "operationType" : NewBodyOperationType.ADD, "depth" : 6.35 * mm});
        }
        {
            var Q0;
            Q0=makeQuery(id+"F46.imprint","IMPRINT",FACE,{"disambiguationData":[TD([[makeQuery(id+"F46.imprint","IMPRINT",EDGE,{"derivedFrom":sQuery(id+"F46.wireOp",EDGE,"E86")}),-1.0]])]});
            extrude(context, id + "F55", {"entities" : qUnion([Q0]), "operationType" : NewBodyOperationType.ADD, "depth" : 6.35 * mm});
        }
        {
            var Q0;
            Q0=makeQuery(id+"F47.imprint","IMPRINT",FACE,{"disambiguationData":[TD([[makeQuery(id+"F47.imprint","IMPRINT",EDGE,{"derivedFrom":sQuery(id+"F47.wireOp",EDGE,"E92")}),-1.0]])]});
            extrude(context, id + "F56", {"entities" : qUnion([Q0]), "operationType" : NewBodyOperationType.ADD, "depth" : 6.35 * mm});
        }
        {
            var Q0;
            Q0=makeQuery(id+"F48.imprint","IMPRINT",FACE,{"disambiguationData":[TD([[makeQuery(id+"F48.imprint","IMPRINT",EDGE,{"derivedFrom":sQuery(id+"F48.wireOp",EDGE,"E98")}),-1.0]])]});
            extrude(context, id + "F57", {"entities" : qUnion([Q0]), "operationType" : NewBodyOperationType.ADD, "depth" : 6.35 * mm});
        }
        {
            var Q0;
            Q0=makeQuery(id+"F49.imprint","IMPRINT",FACE,{"disambiguationData":[TD([[makeQuery(id+"F49.imprint","IMPRINT",EDGE,{"derivedFrom":sQuery(id+"F49.wireOp",EDGE,"E104")}),-1.0]])]});
            extrude(context, id + "F58", {"entities" : qUnion([Q0]), "operationType" : NewBodyOperationType.ADD, "depth" : 6.35 * mm});
        }
        {
            var Q0;
            Q0=makeQuery(id+"F50.imprint","IMPRINT",FACE,{"disambiguationData":[TD([[makeQuery(id+"F50.imprint","IMPRINT",EDGE,{"derivedFrom":sQuery(id+"F50.wireOp",EDGE,"E111")}),1.0]])]});
            extrude(context, id + "F59", {"entities" : qUnion([Q0]), "operationType" : NewBodyOperationType.ADD, "oppositeDirection" : true, "depth" : 6.35 * mm});
        }
    });
